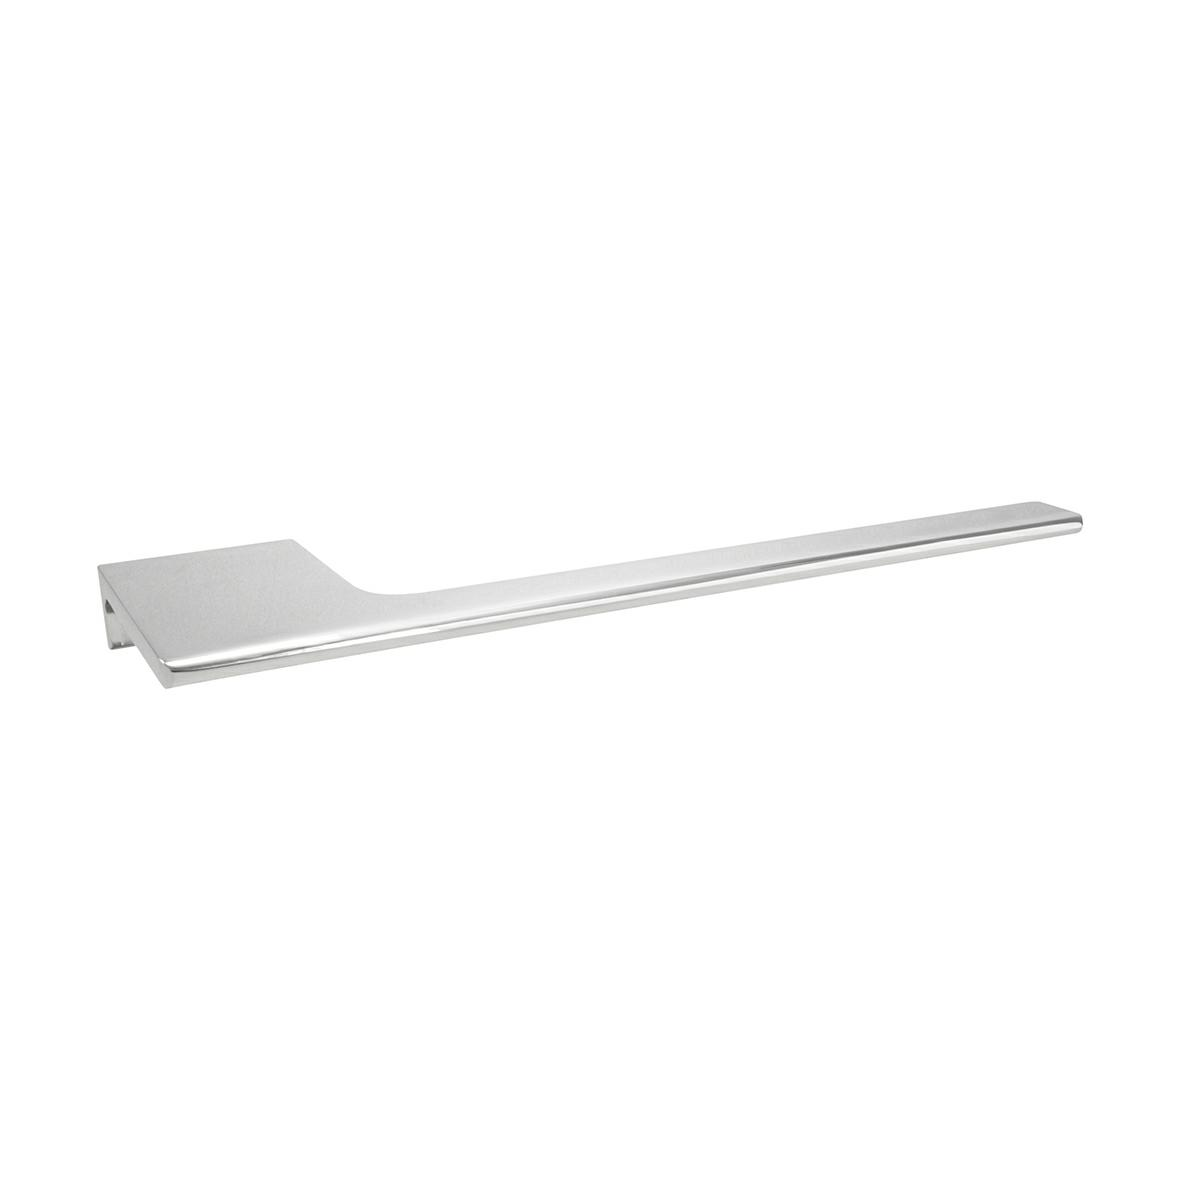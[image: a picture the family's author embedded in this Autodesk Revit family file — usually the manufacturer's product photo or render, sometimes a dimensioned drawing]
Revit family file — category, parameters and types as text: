
# Revit family: ACC-109
name_source: partatom
category: Aparatos sanitarios
units: mm (PartAtom-declared; Revit-internal decimal feet)

## family parameters
Compartido = No
Corte con vacíos al cargar = No
Cota de conector redondo = Diámetro de uso
Número OmniClass = 23.45.00.00
Punto de cálculo de habitación = No
Se basa en plano de trabajo = No
Siempre vertical = Sí
Tipo de pieza = Normal
Título OmniClass = Sanitary, Laundry, and Cleaning Equipment

## types (4) — shared parameters
Brass Chromed = Brass
Comentarios de tipo = Accesories
Elevación por defecto = 0"
Fabricante = HELVEX

## per-type parameters (varying)
| type | Data Sheet | Descripción | Features | Imagen de tipo | Instructive | Total Depth | Total Length | Total Support Diameter | URL | Ébano |
| 14104 | http://helvex.com | Kúbica Paper Holder | Wall Mounted Accessory; Setting Kit Included; Includes Fastening Tool | <Ninguno> | http://helvex.com | 3" | 8" | 2" | http://helvex.com | <Por categoría> |
| ACC-105 | https://www.helvex.com.mx | Toallero de barra Access | Bar towel rack Accessed. | <Ninguno> | https://www.helvex.com.mx | 3" | 24" | 1" | https://www.helvex.com.mx | <Por categoría> |
| ACC-106 | https://www.helvex.com.mx | Gancho sencillo Access | Access simple hook | <Ninguno> | https://www.helvex.com.mx | 3" | 2" | 1" | https://www.helvex.com.mx | <Por categoría> |
| ACC-109 | https://www.helvex.com.mx | Toallero sencillo Access | Accessory single towel rack | ACC-109.jpg | https://www.helvex.com.mx | 1" | 11" | 1" | https://www.helvex.com.mx | Ébano |

note: column(s) folded — value = type name in every type: Modelo

## geometry (parser evidence)
native form markers: Sweep x3
no freeform markers — native parametric forms only
